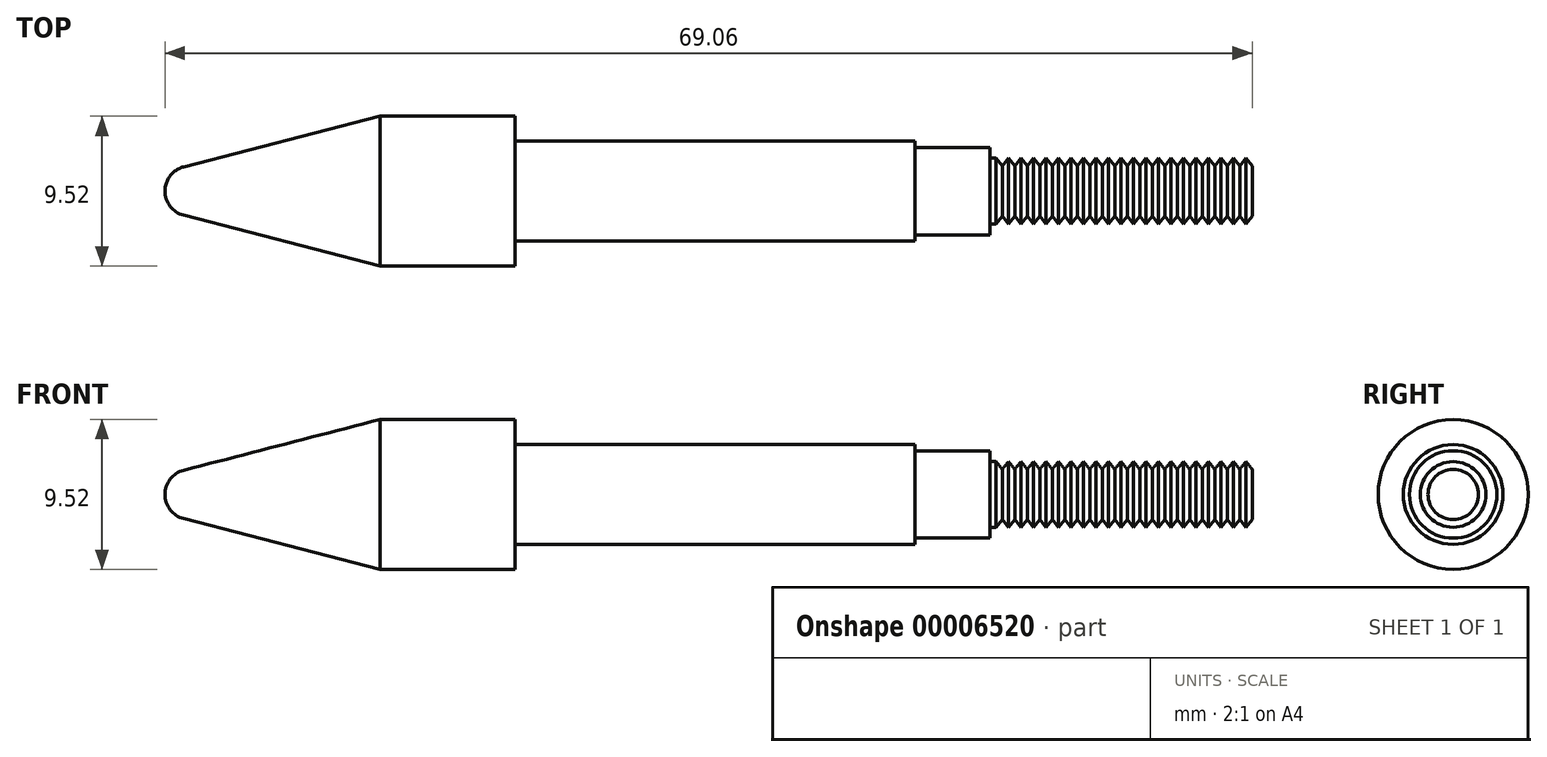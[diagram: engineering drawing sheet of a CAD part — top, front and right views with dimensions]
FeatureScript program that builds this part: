
annotation { "Feature Type Name" : "Feature", "Feature Type Description" : "" }
export const myFeature = defineFeature(function(context is Context, id is Id, definition is map)
    precondition{}
    {
        {
            var Q0;
            Q0=qCreatedBy(makeId("Top.planeOp"),FACE);
            var sketch = newSketch(context, id + "F0", { "sketchPlane" : qUnion([Q0])});
            skLineSegment(sketch, "E0", {"start": v(-98.97, 0) * mm, "end": v(106.84, 0) * mm});
            skLineSegment(sketch, "E1", {"start": v(-23.62, 1.54) * mm, "end": v(-11.14, 4.76) * mm});
            skLineSegment(sketch, "E2", {"start": v(-24.8, 0) * mm, "end": v(-24.8, 9.16) * mm, "construction": true});
            skArc(sketch, "E3", {"start": v(-23.62, 1.54) * mm, "mid": v(-24.47, 0.97) * mm, "end": v(-24.8, 0) * mm});
            skLineSegment(sketch, "E4", {"start": v(-11.14, 4.76) * mm, "end": v(-2.58, 4.76) * mm});
            skLineSegment(sketch, "E5", {"start": v(-2.58, 4.76) * mm, "end": v(-2.58, 3.16) * mm});
            skLineSegment(sketch, "E6", {"start": v(-2.58, 3.16) * mm, "end": v(22.82, 3.16) * mm});
            skLineSegment(sketch, "E7", {"start": v(22.82, 3.16) * mm, "end": v(22.82, 2.78) * mm});
            skLineSegment(sketch, "E8", {"start": v(27.58, 2.08) * mm, "end": v(45.04, 2.08) * mm});
            skLineSegment(sketch, "E9", {"start": v(45.04, 2.08) * mm, "end": v(45.04, 0) * mm});
            skLineSegment(sketch, "E10", {"start": v(27.58, 5.56) * mm, "end": v(27.58, -3.72) * mm, "construction": true});
            skLineSegment(sketch, "E11", {"start": v(20.95, 1.6) * mm, "end": v(46.64, 1.6) * mm, "construction": true});
            skLineSegment(sketch, "E12", {"start": v(45.04, 1.6) * mm, "end": v(44.65, 2.08) * mm});
            skLineSegment(sketch, "E13", {"start": v(44.25, -0.48) * mm, "end": v(44.25, 1.89) * mm});
            skLineSegment(sketch, "E14", {"start": v(44.65, 2.08) * mm, "end": v(44.25, 1.6) * mm});
            skLineSegment(sketch, "E15", {"start": v(22.82, 2.78) * mm, "end": v(27.58, 2.78) * mm});
            skLineSegment(sketch, "E16", {"start": v(27.58, 2.78) * mm, "end": v(27.58, 2.08) * mm});
            skLineSegment(sketch, "E17.1.0.0", {"start": v(44.25, 1.6) * mm, "end": v(43.85, 2.08) * mm});
            skLineSegment(sketch, "E17.1.0.1", {"start": v(43.85, 2.08) * mm, "end": v(43.46, 1.6) * mm});
            skLineSegment(sketch, "E17.1.0.2", {"start": v(-99.76, 0) * mm, "end": v(106.05, 0) * mm});
            skLineSegment(sketch, "E17.2.0.0", {"start": v(43.46, 1.6) * mm, "end": v(43.06, 2.08) * mm});
            skLineSegment(sketch, "E17.2.0.1", {"start": v(43.06, 2.08) * mm, "end": v(42.66, 1.6) * mm});
            skLineSegment(sketch, "E17.2.0.2", {"start": v(-100.56, 0) * mm, "end": v(105.25, 0) * mm});
            skLineSegment(sketch, "E17.3.0.0", {"start": v(42.66, 1.6) * mm, "end": v(42.27, 2.08) * mm});
            skLineSegment(sketch, "E17.3.0.1", {"start": v(42.27, 2.08) * mm, "end": v(41.87, 1.6) * mm});
            skLineSegment(sketch, "E17.3.0.2", {"start": v(-101.35, 0) * mm, "end": v(104.46, 0) * mm});
            skLineSegment(sketch, "E17.4.0.0", {"start": v(41.87, 1.6) * mm, "end": v(41.47, 2.08) * mm});
            skLineSegment(sketch, "E17.4.0.1", {"start": v(41.47, 2.08) * mm, "end": v(41.07, 1.6) * mm});
            skLineSegment(sketch, "E17.4.0.2", {"start": v(-102.15, 0) * mm, "end": v(103.66, 0) * mm});
            skLineSegment(sketch, "E17.5.0.0", {"start": v(41.07, 1.6) * mm, "end": v(40.68, 2.08) * mm});
            skLineSegment(sketch, "E17.5.0.1", {"start": v(40.68, 2.08) * mm, "end": v(40.28, 1.6) * mm});
            skLineSegment(sketch, "E17.5.0.2", {"start": v(-102.94, 0) * mm, "end": v(102.87, 0) * mm});
            skLineSegment(sketch, "E17.6.0.0", {"start": v(40.28, 1.6) * mm, "end": v(39.88, 2.08) * mm});
            skLineSegment(sketch, "E17.6.0.1", {"start": v(39.88, 2.08) * mm, "end": v(39.49, 1.6) * mm});
            skLineSegment(sketch, "E17.6.0.2", {"start": v(-103.73, 0) * mm, "end": v(102.08, 0) * mm});
            skLineSegment(sketch, "E17.7.0.0", {"start": v(39.49, 1.6) * mm, "end": v(39.1, 2.08) * mm});
            skLineSegment(sketch, "E17.7.0.1", {"start": v(39.1, 2.08) * mm, "end": v(38.7, 1.6) * mm});
            skLineSegment(sketch, "E17.7.0.2", {"start": v(-104.53, 0) * mm, "end": v(101.28, 0) * mm});
            skLineSegment(sketch, "E17.8.0.0", {"start": v(38.7, 1.6) * mm, "end": v(38.3, 2.08) * mm});
            skLineSegment(sketch, "E17.8.0.1", {"start": v(38.3, 2.08) * mm, "end": v(37.9, 1.6) * mm});
            skLineSegment(sketch, "E17.8.0.2", {"start": v(-105.32, 0) * mm, "end": v(100.49, 0) * mm});
            skLineSegment(sketch, "E17.9.0.0", {"start": v(37.9, 1.6) * mm, "end": v(37.5, 2.08) * mm});
            skLineSegment(sketch, "E17.9.0.1", {"start": v(37.5, 2.08) * mm, "end": v(37.1, 1.6) * mm});
            skLineSegment(sketch, "E17.9.0.2", {"start": v(-106.11, 0) * mm, "end": v(99.7, 0) * mm});
            skLineSegment(sketch, "E17.10.0.0", {"start": v(37.1, 1.6) * mm, "end": v(36.7, 2.08) * mm});
            skLineSegment(sketch, "E17.10.0.1", {"start": v(36.7, 2.08) * mm, "end": v(36.31, 1.6) * mm});
            skLineSegment(sketch, "E17.10.0.2", {"start": v(-106.9, 0) * mm, "end": v(98.9, 0) * mm});
            skLineSegment(sketch, "E17.11.0.0", {"start": v(36.31, 1.6) * mm, "end": v(35.92, 2.08) * mm});
            skLineSegment(sketch, "E17.11.0.1", {"start": v(35.92, 2.08) * mm, "end": v(35.52, 1.6) * mm});
            skLineSegment(sketch, "E17.11.0.2", {"start": v(-107.7, 0) * mm, "end": v(98.1, 0) * mm});
            skLineSegment(sketch, "E17.12.0.0", {"start": v(35.52, 1.6) * mm, "end": v(35.12, 2.08) * mm});
            skLineSegment(sketch, "E17.12.0.1", {"start": v(35.12, 2.08) * mm, "end": v(34.72, 1.6) * mm});
            skLineSegment(sketch, "E17.12.0.2", {"start": v(-108.5, 0) * mm, "end": v(97.31, 0) * mm});
            skLineSegment(sketch, "E17.13.0.0", {"start": v(34.72, 1.6) * mm, "end": v(34.33, 2.08) * mm});
            skLineSegment(sketch, "E17.13.0.1", {"start": v(34.33, 2.08) * mm, "end": v(33.93, 1.6) * mm});
            skLineSegment(sketch, "E17.13.0.2", {"start": v(-109.29, 0) * mm, "end": v(96.52, 0) * mm});
            skLineSegment(sketch, "E17.14.0.0", {"start": v(33.93, 1.6) * mm, "end": v(33.53, 2.08) * mm});
            skLineSegment(sketch, "E17.14.0.1", {"start": v(33.53, 2.08) * mm, "end": v(33.14, 1.6) * mm});
            skLineSegment(sketch, "E17.14.0.2", {"start": v(-110.08, 0) * mm, "end": v(95.73, 0) * mm});
            skLineSegment(sketch, "E17.15.0.0", {"start": v(33.14, 1.6) * mm, "end": v(32.74, 2.08) * mm});
            skLineSegment(sketch, "E17.15.0.1", {"start": v(32.74, 2.08) * mm, "end": v(32.34, 1.6) * mm});
            skLineSegment(sketch, "E17.15.0.2", {"start": v(-110.88, 0) * mm, "end": v(94.93, 0) * mm});
            skLineSegment(sketch, "E17.16.0.0", {"start": v(32.34, 1.6) * mm, "end": v(31.95, 2.08) * mm});
            skLineSegment(sketch, "E17.16.0.1", {"start": v(31.95, 2.08) * mm, "end": v(31.55, 1.6) * mm});
            skLineSegment(sketch, "E17.16.0.2", {"start": v(-111.67, 0) * mm, "end": v(94.14, 0) * mm});
            skLineSegment(sketch, "E17.17.0.0", {"start": v(31.55, 1.6) * mm, "end": v(31.15, 2.08) * mm});
            skLineSegment(sketch, "E17.17.0.1", {"start": v(31.15, 2.08) * mm, "end": v(30.76, 1.6) * mm});
            skLineSegment(sketch, "E17.17.0.2", {"start": v(-112.46, 0) * mm, "end": v(93.35, 0) * mm});
            skLineSegment(sketch, "E17.18.0.0", {"start": v(30.76, 1.6) * mm, "end": v(30.36, 2.08) * mm});
            skLineSegment(sketch, "E17.18.0.1", {"start": v(30.36, 2.08) * mm, "end": v(29.96, 1.6) * mm});
            skLineSegment(sketch, "E17.18.0.2", {"start": v(-113.26, 0) * mm, "end": v(92.55, 0) * mm});
            skLineSegment(sketch, "E17.19.0.0", {"start": v(29.96, 1.6) * mm, "end": v(29.57, 2.08) * mm});
            skLineSegment(sketch, "E17.19.0.1", {"start": v(29.57, 2.08) * mm, "end": v(29.17, 1.6) * mm});
            skLineSegment(sketch, "E17.19.0.2", {"start": v(-114.05, 0) * mm, "end": v(91.76, 0) * mm});
            skLineSegment(sketch, "E17.20.0.0", {"start": v(29.17, 1.6) * mm, "end": v(28.77, 2.08) * mm});
            skLineSegment(sketch, "E17.20.0.1", {"start": v(28.77, 2.08) * mm, "end": v(28.37, 1.6) * mm});
            skLineSegment(sketch, "E17.20.0.2", {"start": v(-114.85, 0) * mm, "end": v(90.96, 0) * mm});
            skLineSegment(sketch, "E17.21.0.0", {"start": v(28.37, 1.6) * mm, "end": v(27.98, 2.08) * mm});
            skLineSegment(sketch, "E17.21.0.1", {"start": v(27.98, 2.08) * mm, "end": v(27.58, 1.6) * mm});
            skLineSegment(sketch, "E17.21.0.2", {"start": v(-115.64, 0) * mm, "end": v(90.17, 0) * mm});
            skLineSegment(sketch, "E17.direction1", {"start": v(45.04, 1.6) * mm, "end": v(44.25, 1.6) * mm, "construction": true});
            skSolve(sketch);
        }
        {
            var Q0;
            Q0=makeQuery(id+"F0.imprint","IMPRINT",FACE,{"disambiguationData":[TD([[makeQuery(id+"F0.imprint","IMPRINT",EDGE,{"derivedFrom":sQuery(id+"F0.wireOp",EDGE,"E1")}),-1.0]])]});
            var Q1;
            Q1=sQuery(id+"F0.wireOp",EDGE,"E17.16.0.2");
            revolve(context, id + "F1", {"entities" : qUnion([Q0]), "axis" : qUnion([Q1]), "revolveType" : RevolveType.FULL});
        }
    });
